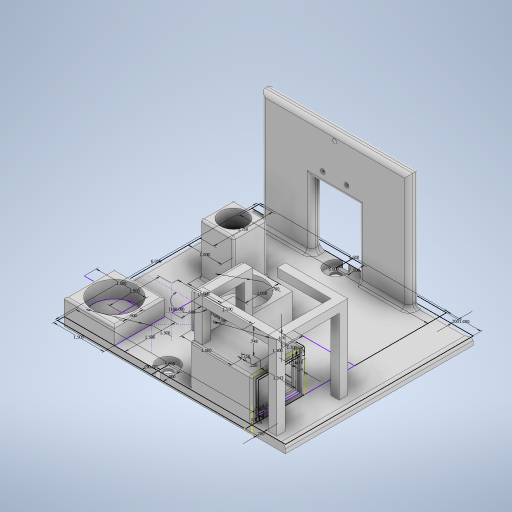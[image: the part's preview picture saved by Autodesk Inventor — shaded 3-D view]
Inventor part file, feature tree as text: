
AUTODESK INVENTOR PART (.ipt)
format: ipt  version: 2024.1 (Build 281209000, 209)  size: 1,398,272 bytes
history: native  units: in
note: dims shown in document units (in); Inventor stores cm internally (conversion verified against a paired STEP export)
features: extrude x20, sketch x10, fillet x7, hole x2
ambient origin geometry x8: Origin, YZ Plane, XZ Plane, XY Plane, X Axis, Y Axis, Z Axis, Center Point
bodies: Solid1 (feature_tree)
feature tree (39):
  sketch  "Sketch1"  dims[d0=5.6in d1=6.0in]
  extrude  "Extrusion1"  Depth=6.0in
  hole  "Hole1"  [1 undecoded]
  extrude  "Extrusion2"  Depth=5.6in
  extrude  "Extrusion3"  Depth=5.6in
  extrude  "Extrusion4"  Depth=0.25in TaperAngle=0.0deg
  extrude  "Extrusion5"  Depth=1.0in
  extrude  "Extrusion6"  Depth=1.5in
  hole  "Hole2"  [1 undecoded]
  extrude  "Extrusion7"  TaperAngle=180.0deg  [1 undecoded]
  extrude  "Extrusion8"  Depth=1.0in
  extrude  "Extrusion9"  Depth=1.0in
  sketch  "Sketch6"  dims[d4=0.5in d5=5.6in]
  extrude  "Extrusion10"  Depth=1.0in
  sketch  "Sketch7"  dims[d6=0.2in d7=5.6in]
  extrude  "Extrusion11"  Depth=1.0in
  extrude  "Extrusion12"  Depth=1.0in
  extrude  "Extrusion13"  Depth=1.0in TaperAngle=0.0deg
  fillet  "Fillet1"  Radius=0.5in
  fillet  "Fillet2"  Radius=1.0in
  fillet  "Fillet3"  Radius=1.5in
  fillet  "Fillet4"  Radius=0.325in
  fillet  "Fillet5"  Radius=2.0in
  fillet  "Fillet6"  Radius=1.5in
  fillet  "Fillet7"  Radius=0.333in
  sketch  "Sketch8"  dims[d8=0.2in d9=0.25in d10=0.0in]
  sketch  "Sketch9"  dims[d11=0.266in d12=0.75in d13=0.625in d14=0.19in d15=0.5635in d16=1.0in d17=0.8108in d18=1.5in]
  extrude  "Extrusion14"  Depth=1.0in
  extrude  "Extrusion15"  Depth=1.0in
  extrude  "Extrusion16"  Depth=1.0in
  extrude  "Extrusion19"  Depth=1.0in
  extrude  "Extrusion17"  Depth=1.0in
  extrude  "Extrusion18"  Depth=1.0in
  extrude  "Extrusion20"  Depth=1.0in
  sketch  "Sketch2"  dims[d2=0.5in d3=90.0deg]
  sketch  "Sketch10"  dims[d19=0.6in d20=1.5in]
  sketch  "Sketch11"  dims[d21=1.5in d22=0.6in]
  sketch  "Sketch13"  dims[d23=1.5in d24=180.0deg]
  sketch  "Sketch14"  dims[d25=1.5in d26=1.5in d27=1.5in d28=1.5in d29=1.3in d30=1.3in d31=0.5in d32=0.0in d33=0.5in d34=0.0in d35=1.0in d36=0.0in d37=1.5in d38=0.325in d39=2.0in d40=0.0in d41=1.5in d42=0.0in d43=0.333in d44=0.96in d45=0.356in d46=0.356in d47=0.134in d48=0.75in d49=0.256in d50=0.118in d51=90.0deg d52=1.0in d53=0.8108in d54=1.75in d55=1.0in d56=1.0in d57=1.0in d58=0.78in d59=1.5in d60=0.0in d61=0.25in d62=0.25in d63=1.5in d64=0.0in d65=1.25in d66=0.0in d67=0.125in d68=0.125in d69=0.125in d70=0.125in d71=1.725in d72=0.0in d73=0.25in d74=0.25in d75=1.043in d76=0.748in d77=0.25in d78=0.0in d79=0.25in d80=0.25in d81=0.0625in d82=0.0625in d83=0.0625in d84=0.0625in d85=0.1875in d86=0.0in d87=0.125in d88=0.0in d89=0.125in d90=0.125in d91=0.0625in d92=0.0625in d93=0.0625in d94=0.0625in d95=0.0625in d96=0.0197in d97=0.0in d98=0.0197in d99=0.0in d100=1.0in d101=0.25in d102=0.25in d103=1.614in d104=90.0deg d105=1.969in d106=0.0in d107=0.25in d108=0.25in d109=0.25in d110=0.25in d111=0.25in d112=0.25in d113=2.5in d114=0.0in d115=0.25in d116=0.25in d117=0.25in d118=0.25in d119=2.5in d120=0.0in d121=2.5in d122=0.0in d123=0.614in d124=90.0deg d125=0.25in d126=0.25in d127=1.0in d128=1.969in d129=0.25in d130=0.25in d131=1.0in d132=90.0deg d133=0.25in d134=2.5in d135=0.0in d136=0.614in d137=1.0in d138=0.0in]
note: 3 required parameter values undecoded (feature->parameter linkage not recoverable at this tier; creation-order binding heuristic only, values carry confidence <= 0.55)
